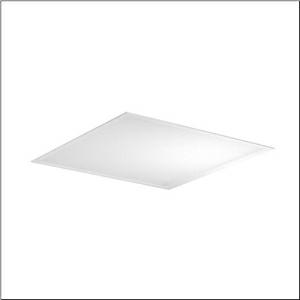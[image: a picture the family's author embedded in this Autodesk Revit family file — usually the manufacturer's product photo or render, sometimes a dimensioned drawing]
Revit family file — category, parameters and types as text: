
# Revit family: apollon_31_square_51mp12wd2442
name_source: partatom
category: Lighting Fixtures
units: mm (PartAtom-declared; Revit-internal decimal feet)

## family parameters
Cut with Voids When Loaded = No
Host = Face
Light Source = No
Part Type = Normal
Room Calculation Point = No
Round Connector Dimension = Use Diameter
Shared = No

## types (1)
- Apollon 31 square (1 x LED, 3800 lm, 27.5 W, 4000K)
    Apparent Load = 28 VA
    CIE Flux Codes = 61 87 97 100 100
    Color Rendering = 80
    Color Temperature = 4000K
    Default Elevation = 1800 mm
    Description = Apollon 31 square, office luminaire, primary optical cover: micro prismatic cover, of PMMA, CAT 2 (L<= 3000cd/m²), light emission: direct distribution, primary light characteristic: symmetric, installation type: lay-in mounting, recessed, LED, rated luminous flux: 3.800lm, luminous efficacy: 138lm/W, light colour: 840, colour temperature: 4000K, control gear: DALI 2, Multilumen, with terminal, 5-pole, mains connection: 220..240V, AC/DC, 0/50..60Hz, rated input power: 28W, suitable for self-contained emergency lighting element 58DB00B013A with integrated self-test function according to EN 60598-2-22, housing, of aluminium, coated, traffic white (RAL 9016), module: M600, length: 595mm, width: 595mm, height: 62mm, housing upper side, of sheet steel, coated, protection rating (complete): IP20, protection rating (lamp compartment, on room side): IP40, insulation class (complete): insulation class II (safety insulation), certification: CE, ENEC, impact resistance: IK03, permissible operating ambient temperature: -20..+40°C, standard: EN 60598-2-22, corresponds to IFS (International Featured Standards) requirements for safety and quality in the food industry, packaging unit: 1 piece
    Height = 0 mm  [stored 0 ft]
    Lamp = 1 x LED
    Lamp Light Flux = 3800 lm
    Lamp Power = 27.5 W
    Lamp count = 1
    Length = 595 mm
    Luminous efficacy = 138 lm/W
    Manufacturer = Siteco
    ModVariant = No
    Model = 51MP12WD2442
    Mounting Place = Ceiling
    Mounting Type = Recessed
    Number of Poles = 1
    OnlyDefault = Yes
    Power Factor = 1
    Product Name = Apollon 31 square
    Product group = office luminaire | ceiling recessed
    ProductGroupID = 400
    Protection Class = Protection class II
    Protection Degree = IP 20
    RLX_Detail_Level = 1
    RLX_Emergency_Light_Flux = 0 lm
    RLX_Emergency_Type = 0
    RLX_Emergency_Type_DB = No
    RlxData = <blob elided: 12837 chars, md5=c8b2bb17>
    Socket = socket
    Standby Power = 0 W
    System Light Flux = 3800 lm
    System Power = 28 W
    Type Comments = Product without accessories
    Type Image = l_1291035.jpg
    URL = http://relux.com
    VarID = ---
    Voltage = 0 V
    Weight = 0.00 kg
    Width = 595 mm

note: [stored X ft] marks values corroborated as IEEE doubles in the binary element streams (Revit-internal decimal feet)

## geometry (parser evidence)
native form markers: Sweep x9
no freeform markers — native parametric forms only
